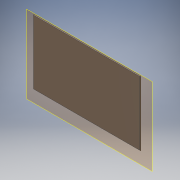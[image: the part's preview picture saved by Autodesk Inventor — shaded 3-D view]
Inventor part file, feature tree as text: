
AUTODESK INVENTOR PART (.ipt)
format: ipt  version: 2016 SP2 (Build 200236200, 236)  size: 95,232 bytes
history: native  units: mm
features: other x3, sketch x1, plane x1
ambient origin geometry x8: Origin, YZ Plane, XZ Plane, XY Plane, X Axis, Y Axis, Z Axis, Center Point
bodies: Volumenkörper1 (feature_tree)
feature tree (5):
  other  "Zwischenplatt.ipt"
  other  "Volumenkörper2::Zwischenplatt.ipt"
  other  "Bezeichnung1"
  sketch  "Skizze2"  dims[d0=10.0mm]
  plane  "Arbeitsebene1"
